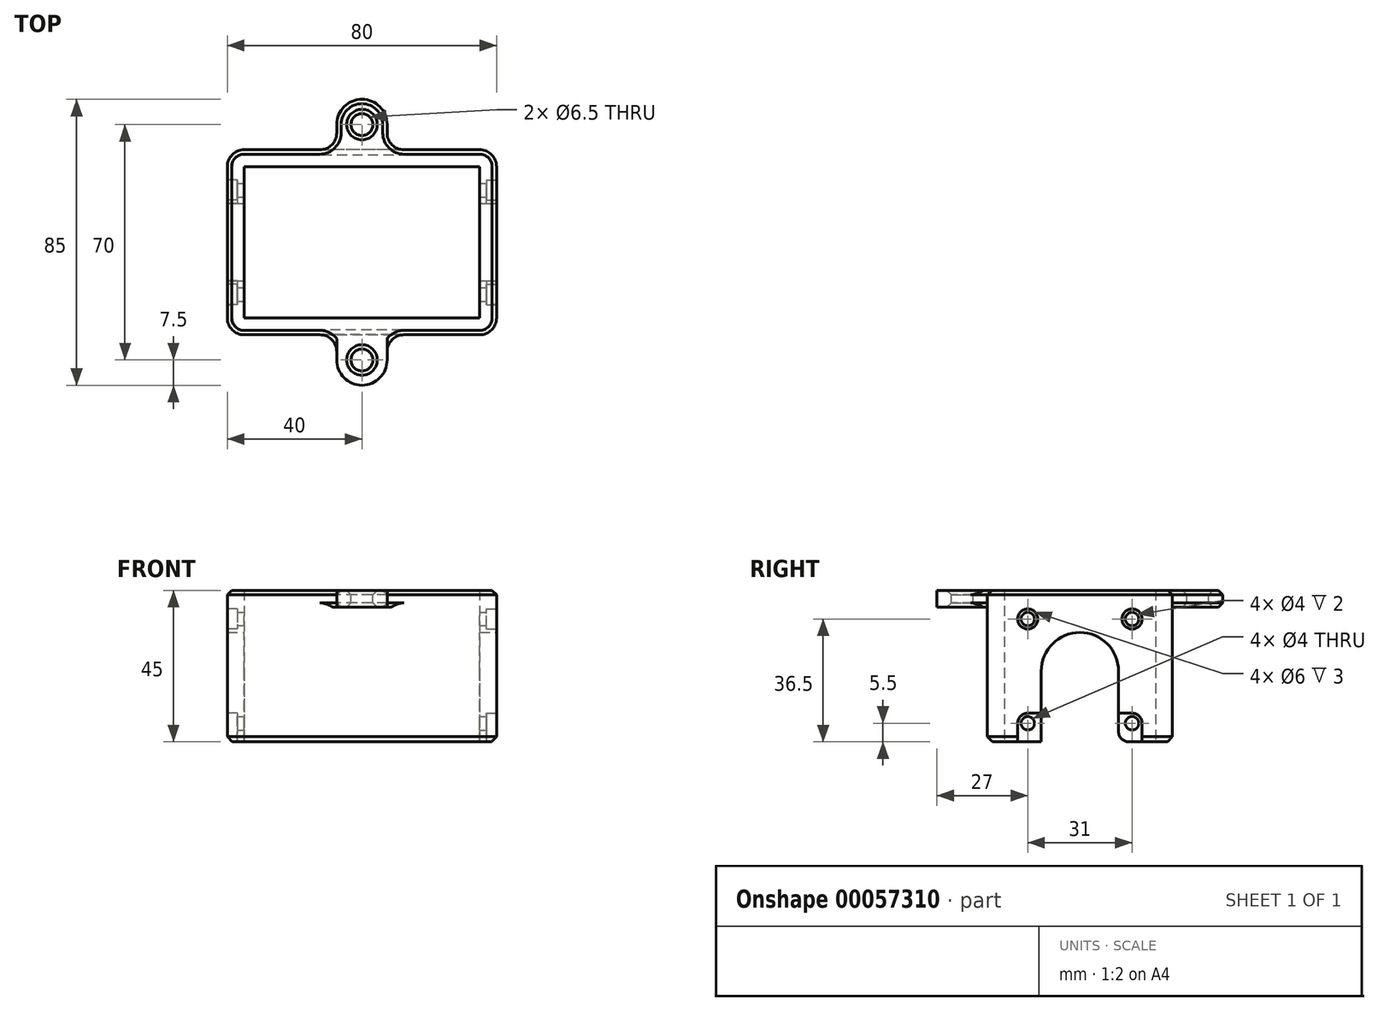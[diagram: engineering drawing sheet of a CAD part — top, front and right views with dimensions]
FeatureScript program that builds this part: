
annotation { "Feature Type Name" : "Feature", "Feature Type Description" : "" }
export const myFeature = defineFeature(function(context is Context, id is Id, definition is map)
    precondition{}
    {
        {
            var Q0;
            Q0=qCreatedBy(makeId("Top.planeOp"),FACE);
            var sketch = newSketch(context, id + "F0", { "sketchPlane" : qUnion([Q0])});
            skLineSegment(sketch, "E0.rect.bottom", {"start": v(35, 22.5) * mm, "end": v(-35, 22.5) * mm});
            skLineSegment(sketch, "E0.rect.top", {"start": v(35, -22.5) * mm, "end": v(-35, -22.5) * mm});
            skLineSegment(sketch, "E0.rect.left", {"start": v(35, 22.5) * mm, "end": v(35, -22.5) * mm});
            skLineSegment(sketch, "E0.rect.right", {"start": v(-35, 22.5) * mm, "end": v(-35, -22.5) * mm});
            skPoint(sketch, "E0.rect.middle", {"position": v(0, 0) * mm});
            skLineSegment(sketch, "E1.0", {"start": v(35, 27.5) * mm, "end": v(-35, 27.5) * mm});
            skLineSegment(sketch, "E1.1", {"start": v(40, 22.5) * mm, "end": v(40, -22.5) * mm});
            skLineSegment(sketch, "E1.2", {"start": v(35, -27.5) * mm, "end": v(-35, -27.5) * mm});
            skLineSegment(sketch, "E1.3", {"start": v(-40, 22.5) * mm, "end": v(-40, -22.5) * mm});
            skPoint(sketch, "E2.visualSharp", {"position": v(-40, 27.5) * mm});
            skArc(sketch, "E2.filletArc", {"start": v(-35, 27.5) * mm, "mid": v(-38.54, 26.04) * mm, "end": v(-40, 22.5) * mm});
            skPoint(sketch, "E3.visualSharp", {"position": v(-40, -27.5) * mm});
            skArc(sketch, "E3.filletArc", {"start": v(-40, -22.5) * mm, "mid": v(-38.54, -26.04) * mm, "end": v(-35, -27.5) * mm});
            skPoint(sketch, "E4.visualSharp", {"position": v(40, -27.5) * mm});
            skArc(sketch, "E4.filletArc", {"start": v(35, -27.5) * mm, "mid": v(38.54, -26.04) * mm, "end": v(40, -22.5) * mm});
            skPoint(sketch, "E5.visualSharp", {"position": v(40, 27.5) * mm});
            skArc(sketch, "E5.filletArc", {"start": v(40, 22.5) * mm, "mid": v(38.54, 26.04) * mm, "end": v(35, 27.5) * mm});
            skSolve(sketch);
        }
        {
            var Q0;
            Q0=makeQuery(id+"F0.imprint","IMPRINT",FACE,{"disambiguationData":[TD([[makeQuery(id+"F0.imprint","IMPRINT",EDGE,{"derivedFrom":sQuery(id+"F0.wireOp",EDGE,"E0.rect.bottom")}),-1.0]])]});
            extrude(context, id + "F1", {"entities" : qUnion([Q0]), "depth" : 45 * mm});
        }
        {
            var Q0;
            Q0=qCreatedBy(makeId("Right.planeOp"),FACE);
            var sketch = newSketch(context, id + "F2", { "sketchPlane" : qUnion([Q0])});
            skCircle(sketch, "E6", {"center": v(0, 21) * mm, "radius": 11.5 * mm, "construction": true});
            skLineSegment(sketch, "E7.rect.bottom", {"start": v(-15.5, 5.5) * mm, "end": v(15.5, 5.5) * mm, "construction": true});
            skLineSegment(sketch, "E7.rect.top", {"start": v(-15.5, 36.5) * mm, "end": v(15.5, 36.5) * mm, "construction": true});
            skLineSegment(sketch, "E7.rect.left", {"start": v(-15.5, 5.5) * mm, "end": v(-15.5, 36.5) * mm, "construction": true});
            skLineSegment(sketch, "E7.rect.right", {"start": v(15.5, 5.5) * mm, "end": v(15.5, 36.5) * mm, "construction": true});
            skCircle(sketch, "E8", {"center": v(15.5, 36.5) * mm, "radius": 2 * mm});
            skCircle(sketch, "E9", {"center": v(-15.5, 36.5) * mm, "radius": 2 * mm});
            skCircle(sketch, "E10", {"center": v(15.5, 5.5) * mm, "radius": 2 * mm});
            skCircle(sketch, "E11", {"center": v(-15.5, 5.5) * mm, "radius": 2 * mm});
            skLineSegment(sketch, "E12", {"start": v(11.5, 21) * mm, "end": v(11.5, 0) * mm});
            skLineSegment(sketch, "E13", {"start": v(11.5, 0) * mm, "end": v(-11.5, 0) * mm});
            skLineSegment(sketch, "E14", {"start": v(-11.5, 0) * mm, "end": v(-11.5, 21) * mm});
            skArc(sketch, "E15", {"start": v(11.5, 21) * mm, "mid": v(0, 32.5) * mm, "end": v(-11.5, 21) * mm});
            skSolve(sketch);
        }
        {
            var Q0;
            Q0 = qSketchRegion(id + "F2", true);
            extrude(context, id + "F3", {"entities" : qUnion([Q0]), "operationType" : NewBodyOperationType.REMOVE, "endBound" : BoundingType.THROUGH_ALL, "oppositeDirection" : true, "depth" : 25 * mm, "hasSecondDirection" : true, "secondDirectionBound" : SecondDirectionBoundingType.THROUGH_ALL, "secondDirectionOppositeDirection" : false, "secondDirectionDepth" : 25 * mm});
        }
        {
            var Q0;
            Q0=qCreatedBy(makeId("Right.planeOp"),FACE);
            var sketch = newSketch(context, id + "F4", { "sketchPlane" : qUnion([Q0])});
            skCircle(sketch, "E16", {"center": v(-15.5, 36.5) * mm, "radius": 3 * mm});
            skCircle(sketch, "E17", {"center": v(-15.5, 5.5) * mm, "radius": 3 * mm, "construction": true});
            skLineSegment(sketch, "E18", {"start": v(-18.5, 5.5) * mm, "end": v(-18.5, 0) * mm});
            skLineSegment(sketch, "E19", {"start": v(-18.5, 0) * mm, "end": v(-11.5, 0) * mm});
            skLineSegment(sketch, "E20", {"start": v(-15.5, 8.5) * mm, "end": v(-11.5, 8.5) * mm});
            skLineSegment(sketch, "E21", {"start": v(-11.5, 8.5) * mm, "end": v(-11.5, 0) * mm});
            skArc(sketch, "E22", {"start": v(-15.5, 8.5) * mm, "mid": v(-17.62, 7.62) * mm, "end": v(-18.5, 5.5) * mm});
            skCircle(sketch, "E23.MirrorC", {"center": v(15.5, 36.5) * mm, "radius": 3 * mm});
            skArc(sketch, "E24.MirrorCS", {"start": v(15.5, 8.5) * mm, "mid": v(17.62, 7.62) * mm, "end": v(18.5, 5.5) * mm});
            skLineSegment(sketch, "E25.MirrorCS", {"start": v(15.5, 8.5) * mm, "end": v(11.5, 8.5) * mm});
            skLineSegment(sketch, "E26.MirrorCS", {"start": v(11.5, 8.5) * mm, "end": v(11.5, 0) * mm});
            skLineSegment(sketch, "E27.MirrorCS", {"start": v(18.5, 5.5) * mm, "end": v(18.5, 0) * mm});
            skLineSegment(sketch, "E28.MirrorCS", {"start": v(18.5, 0) * mm, "end": v(11.5, 0) * mm});
            skSolve(sketch);
        }
        {
            var Q0;
            Q0=makeQuery(id+"F1.opExtrude","SWEPT_FACE",FACE,{"disambiguationData":[OSD([sQuery(id+"F0.wireOp",EDGE,"E1.1")])]});
            var sketch = newSketch(context, id + "F5", { "sketchPlane" : qUnion([Q0])});
            skCircle(sketch, "E29.0", {"center": v(-15.5, 36.5) * mm, "radius": 3 * mm});
            skCircle(sketch, "E30.0", {"center": v(15.5, 36.5) * mm, "radius": 3 * mm});
            skLineSegment(sketch, "E31.0", {"start": v(-18.5, 5.5) * mm, "end": v(-18.5, 0) * mm});
            skArc(sketch, "E32.0", {"start": v(-15.5, 8.5) * mm, "mid": v(-17.62, 7.62) * mm, "end": v(-18.5, 5.5) * mm});
            skLineSegment(sketch, "E33.0", {"start": v(-15.5, 8.5) * mm, "end": v(-11.5, 8.5) * mm});
            skLineSegment(sketch, "E34.0", {"start": v(-11.5, 8.5) * mm, "end": v(-11.5, 0) * mm});
            skLineSegment(sketch, "E35.0", {"start": v(-18.5, 0) * mm, "end": v(-11.5, 0) * mm});
            skLineSegment(sketch, "E36.0", {"start": v(11.5, 8.5) * mm, "end": v(11.5, 0) * mm});
            skLineSegment(sketch, "E37.0", {"start": v(15.5, 8.5) * mm, "end": v(11.5, 8.5) * mm});
            skArc(sketch, "E38.0", {"start": v(15.5, 8.5) * mm, "mid": v(17.62, 7.62) * mm, "end": v(18.5, 5.5) * mm});
            skLineSegment(sketch, "E39.0", {"start": v(18.5, 5.5) * mm, "end": v(18.5, 0) * mm});
            skLineSegment(sketch, "E40.0", {"start": v(18.5, 0) * mm, "end": v(11.5, 0) * mm});
            skSolve(sketch);
        }
        {
            var Q0;
            Q0 = qSketchRegion(id + "F5", true);
            extrude(context, id + "F6", {"entities" : qUnion([Q0]), "operationType" : NewBodyOperationType.REMOVE, "oppositeDirection" : true, "depth" : 3 * mm});
        }
        {
            var Q0;
            Q0=makeQuery(id+"F1.opExtrude","SWEPT_FACE",FACE,{"disambiguationData":[OSD([sQuery(id+"F0.wireOp",EDGE,"E1.3")])]});
            var sketch = newSketch(context, id + "F7", { "sketchPlane" : qUnion([Q0])});
            skCircle(sketch, "E41.0", {"center": v(-15.5, 36.5) * mm, "radius": 3 * mm});
            skCircle(sketch, "E42.0", {"center": v(15.5, 36.5) * mm, "radius": 3 * mm});
            skLineSegment(sketch, "E43.0", {"start": v(18.5, 0) * mm, "end": v(11.5, 0) * mm});
            skLineSegment(sketch, "E44.0", {"start": v(18.5, 5.5) * mm, "end": v(18.5, 0) * mm});
            skArc(sketch, "E45.0", {"start": v(15.5, 8.5) * mm, "mid": v(17.62, 7.62) * mm, "end": v(18.5, 5.5) * mm});
            skLineSegment(sketch, "E46.0", {"start": v(15.5, 8.5) * mm, "end": v(11.5, 8.5) * mm});
            skLineSegment(sketch, "E47.0", {"start": v(11.5, 8.5) * mm, "end": v(11.5, 0) * mm});
            skArc(sketch, "E48.0", {"start": v(-15.5, 8.5) * mm, "mid": v(-17.62, 7.62) * mm, "end": v(-18.5, 5.5) * mm});
            skLineSegment(sketch, "E49.0", {"start": v(-15.5, 8.5) * mm, "end": v(-11.5, 8.5) * mm});
            skLineSegment(sketch, "E50.0", {"start": v(-11.5, 8.5) * mm, "end": v(-11.5, 0) * mm});
            skLineSegment(sketch, "E51.0", {"start": v(-18.5, 0) * mm, "end": v(-11.5, 0) * mm});
            skLineSegment(sketch, "E52.0", {"start": v(-18.5, 5.5) * mm, "end": v(-18.5, 0) * mm});
            skSolve(sketch);
        }
        {
            var Q0;
            Q0 = qSketchRegion(id + "F7", true);
            extrude(context, id + "F8", {"entities" : qUnion([Q0]), "operationType" : NewBodyOperationType.REMOVE, "oppositeDirection" : true, "depth" : 3 * mm});
        }
        {
            var Q0;
            Q0=makeQuery(id+"F3.boolean.opBoolean","COPY",EDGE,{"disambiguationData":[OD(1.0)],"derivedFrom":makeQuery(id+"F3.opExtrude","SWEPT_EDGE",EDGE,{"disambiguationData":[OSD([sQuery(id+"F2.wireOp",EDGE,"E12"),sQuery(id+"F2.wireOp",EDGE,"E13")])]})});
            var Q1;
            Q1=makeQuery(id+"F3.boolean.opBoolean","COPY",EDGE,{"disambiguationData":[OD(1.0)],"derivedFrom":makeQuery(id+"F3.opExtrude","SWEPT_EDGE",EDGE,{"disambiguationData":[OSD([sQuery(id+"F2.wireOp",EDGE,"E13"),sQuery(id+"F2.wireOp",EDGE,"E14")])]})});
            var Q2;
            Q2=makeQuery(id+"F3.boolean.opBoolean","COPY",EDGE,{"disambiguationData":[OD(0.0)],"derivedFrom":makeQuery(id+"F3.opExtrude","SWEPT_EDGE",EDGE,{"disambiguationData":[OSD([sQuery(id+"F2.wireOp",EDGE,"E13"),sQuery(id+"F2.wireOp",EDGE,"E14")])]})});
            var Q3;
            Q3=makeQuery(id+"F3.boolean.opBoolean","COPY",EDGE,{"disambiguationData":[OD(0.0)],"derivedFrom":makeQuery(id+"F3.opExtrude","SWEPT_EDGE",EDGE,{"disambiguationData":[OSD([sQuery(id+"F2.wireOp",EDGE,"E12"),sQuery(id+"F2.wireOp",EDGE,"E13")])]})});
            fillet(context, id + "F9", {"entities" : qUnion([Q0, Q1, Q2, Q3]), "radius" : 3 * mm, "tangentPropagation" : true, "allowEdgeOverflow" : false});
        }
        {
            var Q0;
            {var subQ0=sQuery(id+"F0.wireOp",EDGE,"E2.filletArc");var subQ1=sQuery(id+"F0.wireOp",EDGE,"E1.3");Q0=makeQuery(id+"F3.boolean.opBoolean","SPLIT",EDGE,{"disambiguationData":[TD([makeQuery(id+"F1.opExtrude","SWEPT_FACE",FACE,{"disambiguationData":[OSD([subQ0])]})])],"derivedFrom":makeQuery(id+"F1.opExtrude","CAP_EDGE",EDGE,{"disambiguationData":[OSD([subQ1])],"isStart":true})});}
            var Q1;
            Q1=makeQuery(id+"F1.opExtrude","CAP_EDGE",EDGE,{"disambiguationData":[OSD([sQuery(id+"F0.wireOp",EDGE,"E3.filletArc")])],"isStart":true});
            chamfer(context, id + "F10", {"entities" : qUnion([Q0, Q1]), "width" : 1.5 * mm, "tangentPropagation" : true});
        }
        {
            var Q0;
            Q0=makeQuery(id+"F1.opExtrude","CAP_FACE",FACE,{"disambiguationData":[OSD([sQuery(id+"F0.wireOp",EDGE,"E0.rect.bottom"),sQuery(id+"F0.wireOp",EDGE,"E0.rect.top"),sQuery(id+"F0.wireOp",EDGE,"E0.rect.left"),sQuery(id+"F0.wireOp",EDGE,"E0.rect.right"),sQuery(id+"F0.wireOp",EDGE,"E1.0"),sQuery(id+"F0.wireOp",EDGE,"E1.1"),sQuery(id+"F0.wireOp",EDGE,"E1.2"),sQuery(id+"F0.wireOp",EDGE,"E1.3"),sQuery(id+"F0.wireOp",EDGE,"E2.filletArc"),sQuery(id+"F0.wireOp",EDGE,"E3.filletArc"),sQuery(id+"F0.wireOp",EDGE,"E4.filletArc"),sQuery(id+"F0.wireOp",EDGE,"E5.filletArc")])],"isStart":false});
            var sketch = newSketch(context, id + "F11", { "sketchPlane" : qUnion([Q0])});
            skCircle(sketch, "E53", {"center": v(0, 35) * mm, "radius": 3.25 * mm});
            skCircle(sketch, "E54", {"center": v(0, -35) * mm, "radius": 3.25 * mm});
            skArc(sketch, "E55", {"start": v(7.5, 35) * mm, "mid": v(0, 42.5) * mm, "end": v(-7.5, 35) * mm});
            skArc(sketch, "E56", {"start": v(-7.5, -35) * mm, "mid": v(0, -42.5) * mm, "end": v(7.5, -35) * mm});
            skLineSegment(sketch, "E57", {"start": v(0, 35) * mm, "end": v(0, -35) * mm});
            skLineSegment(sketch, "E58", {"start": v(-7.5, 35) * mm, "end": v(-7.5, 27.5) * mm});
            skLineSegment(sketch, "E59", {"start": v(7.5, 35) * mm, "end": v(7.5, 27.5) * mm});
            skLineSegment(sketch, "E60", {"start": v(-7.5, 27.5) * mm, "end": v(7.5, 27.5) * mm});
            skLineSegment(sketch, "E61", {"start": v(-7.5, -22.5) * mm, "end": v(7.5, -22.5) * mm});
            skLineSegment(sketch, "E62.trimOffspring", {"start": v(-7.5, -22.5) * mm, "end": v(-7.5, -35) * mm});
            skLineSegment(sketch, "E63.trimOffspring", {"start": v(7.5, -22.5) * mm, "end": v(7.5, -35) * mm});
            skSolve(sketch);
        }
        {
            var Q0;
            Q0 = qSketchRegion(id + "F11", true);
            extrude(context, id + "F12", {"entities" : qUnion([Q0]), "operationType" : NewBodyOperationType.ADD, "oppositeDirection" : true, "depth" : 5 * mm});
        }
        {
            var Q0;
            Q0=makeQuery(id+"F12.opExtrude","SWEPT_EDGE",EDGE,{"disambiguationData":[OSD([sQuery(id+"F0.wireOp",EDGE,"E1.0"),sQuery(id+"F11.wireOp",EDGE,"E59"),sQuery(id+"F11.wireOp",EDGE,"E60")])]});
            var Q1;
            Q1=makeQuery(id+"F12.opExtrude","SWEPT_EDGE",EDGE,{"disambiguationData":[OSD([sQuery(id+"F0.wireOp",EDGE,"E1.0"),sQuery(id+"F11.wireOp",EDGE,"E58"),sQuery(id+"F11.wireOp",EDGE,"E60")])]});
            var Q2;
            Q2=makeQuery(id+"F12.boolean.opBoolean","INTERSECT",EDGE,{"derivedFrom":[makeQuery(id+"F1.opExtrude","SWEPT_FACE",FACE,{"disambiguationData":[OSD([sQuery(id+"F0.wireOp",EDGE,"E1.2")])]}),makeQuery(id+"F12.opExtrude","SWEPT_FACE",FACE,{"disambiguationData":[OSD([sQuery(id+"F11.wireOp",EDGE,"E62.trimOffspring")])]})]});
            var Q3;
            Q3=makeQuery(id+"F12.boolean.opBoolean","INTERSECT",EDGE,{"derivedFrom":[makeQuery(id+"F1.opExtrude","SWEPT_FACE",FACE,{"disambiguationData":[OSD([sQuery(id+"F0.wireOp",EDGE,"E1.2")])]}),makeQuery(id+"F12.opExtrude","SWEPT_FACE",FACE,{"disambiguationData":[OSD([sQuery(id+"F11.wireOp",EDGE,"E63.trimOffspring")])]})]});
            fillet(context, id + "F13", {"entities" : qUnion([Q0, Q1, Q2, Q3]), "radius" : 5 * mm, "tangentPropagation" : true, "allowEdgeOverflow" : false});
        }
        {
            var Q0;
            {var subQ1=sQuery(id+"F0.wireOp",EDGE,"E4.filletArc");var subQ2=sQuery(id+"F0.wireOp",EDGE,"E1.2");Q0=makeQuery(id+"F12.boolean.opBoolean","SPLIT",EDGE,{"disambiguationData":[TD([makeQuery(id+"F1.opExtrude","SWEPT_FACE",FACE,{"disambiguationData":[OSD([subQ1])]})])],"derivedFrom":makeQuery(id+"F1.opExtrude","CAP_EDGE",EDGE,{"disambiguationData":[OSD([subQ2])],"isStart":false})});}
            var Q1;
            Q1=makeQuery(id+"F12.opExtrude","CAP_EDGE",EDGE,{"disambiguationData":[OSD([sQuery(id+"F11.wireOp",EDGE,"E54")])],"isStart":true});
            var Q2;
            Q2=makeQuery(id+"F12.opExtrude","CAP_EDGE",EDGE,{"disambiguationData":[OSD([sQuery(id+"F11.wireOp",EDGE,"E53")])],"isStart":true});
            var Q3;
            Q3=makeQuery(id+"F12.opExtrude","CAP_EDGE",EDGE,{"disambiguationData":[OSD([sQuery(id+"F11.wireOp",EDGE,"E55")])],"isStart":false});
            var Q4;
            Q4=makeQuery(id+"F12.opExtrude","CAP_EDGE",EDGE,{"disambiguationData":[OSD([sQuery(id+"F11.wireOp",EDGE,"E53")])],"isStart":false});
            var Q5;
            {var subQ0=sQuery(id+"F11.wireOp",EDGE,"E62.trimOffspring");Q5=makeQuery(id+"F13.opFillet","BLEND_EDGE",EDGE,{"blendedFrom":[makeQuery(id+"F12.boolean.opBoolean","INTERSECT",EDGE,{"derivedFrom":[makeQuery(id+"F1.opExtrude","SWEPT_FACE",FACE,{"disambiguationData":[OSD([sQuery(id+"F0.wireOp",EDGE,"E1.2")])]}),makeQuery(id+"F12.opExtrude","SWEPT_FACE",FACE,{"disambiguationData":[OSD([subQ0])]})]}),makeQuery(id+"F12.opExtrude","CAP_FACE",FACE,{"disambiguationData":[OSD([sQuery(id+"F11.wireOp",EDGE,"E54"),sQuery(id+"F11.wireOp",EDGE,"E56"),sQuery(id+"F11.wireOp",EDGE,"E61"),subQ0,sQuery(id+"F11.wireOp",EDGE,"E63.trimOffspring")])],"isStart":false})],"blendedInto":[makeQuery(id+"F12.opExtrude","CAP_FACE",FACE,{"disambiguationData":[OSD([sQuery(id+"F11.wireOp",EDGE,"E54"),sQuery(id+"F11.wireOp",EDGE,"E56"),sQuery(id+"F11.wireOp",EDGE,"E61"),subQ0,sQuery(id+"F11.wireOp",EDGE,"E63.trimOffspring")])],"isStart":false})]});}
            var Q6;
            Q6=makeQuery(id+"F12.opExtrude","CAP_EDGE",EDGE,{"disambiguationData":[OSD([sQuery(id+"F11.wireOp",EDGE,"E54")])],"isStart":false});
            chamfer(context, id + "F14", {"entities" : qUnion([Q0, Q1, Q2, Q3, Q4, Q5, Q6]), "width" : 1.3 * mm, "tangentPropagation" : true});
        }
    });
